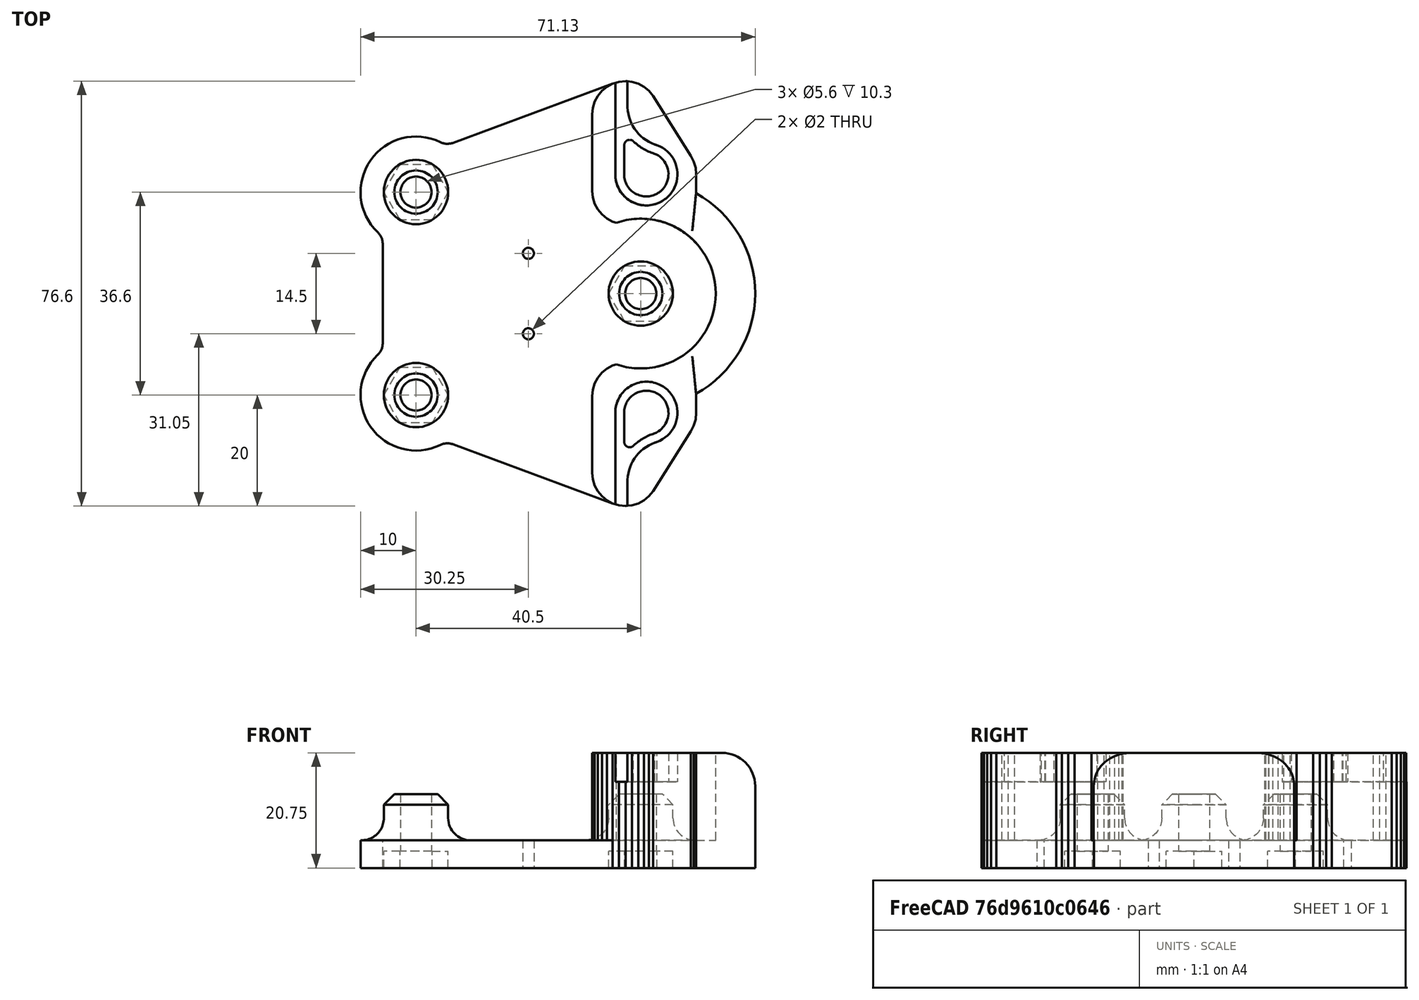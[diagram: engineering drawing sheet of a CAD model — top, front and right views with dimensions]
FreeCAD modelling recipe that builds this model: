
FCSTD DOCUMENT  (FreeCAD 0.19R24267 +99 (Git))
Label: carroX_V1
License: All rights reserved
LicenseURL: http://en.wikipedia.org/wiki/All_rights_reserved
objects: Part::Feature×137, Part::Part2DObjectPython×11, Part::Cylinder×9, Part::FeaturePython×8, Part::Cut×7, Part::MultiFuse×5, Part::Extrusion×5, Part::Prism×3, Part::Fillet×3, Part::Fuse×2, Part::Box×1, App::DocumentObjectGroupPython×1, Part::Mirroring×1, Part::Refine×1, Part::Chamfer×1
note: 194 computed .brp shape members not serialized (recipe doc carries the construction recipe); baked Part::Feature solids carry a one-line shape summary decoded from their .brp

FEATURE [Part::Feature] polygon
  shape: bbox 44.5 x 64.6 x 2e-07 mm, 1 faces, 0 solids (baked)
FEATURE [Part::Part2DObjectPython] circle  # Draft 2D object (typed FeaturePython)
  Area = 113.097
  FirstAngle = 0
  LastAngle = 0
  MakeFace = true
  Radius = 6
FEATURE [Part::FeaturePython] minkowski  # WARN: FeaturePython — macro-defined, semantics opaque (R4)
  Arguments = {'convexity': '0'}
  Children = -> [polygon,circle]
  Operation = minkowski
FEATURE [Part::Part2DObjectPython] circle001  # Draft 2D object (typed FeaturePython)
  Area = 314.159
  FirstAngle = 0
  LastAngle = 0
  MakeFace = true
  Placement = pos=(-20.25,-18.3,0) rot=(0,0,1;0rad)
  Radius = 10
FEATURE [Part::Part2DObjectPython] circle002  # Draft 2D object (typed FeaturePython)
  Area = 314.159
  FirstAngle = 0
  LastAngle = 0
  MakeFace = true
  Placement = pos=(-20.25,18.3,0) rot=(0,0,1;0rad)
  Radius = 10
FEATURE [Part::Part2DObjectPython] circle003  # Draft 2D object (typed FeaturePython)
  Area = 1336.4
  FirstAngle = 0
  LastAngle = 0
  MakeFace = true
  Placement = pos=(20.25,0,0) rot=(0,0,1;0rad)
  Radius = 20.625
FEATURE [Part::MultiFuse] union
  Shapes = -> [minkowski,circle001,circle002,circle003]
FEATURE [Part::Part2DObjectPython] circle004  # Draft 2D object (typed FeaturePython)
  Area = 24.6301
  FirstAngle = 0
  LastAngle = 0
  MakeFace = true
  Placement = pos=(-20.25,-18.3,0) rot=(0,0,1;0rad)
  Radius = 2.8
FEATURE [Part::Part2DObjectPython] circle005  # Draft 2D object (typed FeaturePython)
  Area = 24.6301
  FirstAngle = 0
  LastAngle = 0
  MakeFace = true
  Placement = pos=(20.25,0,0) rot=(0,0,1;0rad)
  Radius = 2.8
FEATURE [Part::Part2DObjectPython] circle006  # Draft 2D object (typed FeaturePython)
  Area = 24.6301
  FirstAngle = 0
  LastAngle = 0
  MakeFace = true
  Placement = pos=(-20.25,18.3,0) rot=(0,0,1;0rad)
  Radius = 2.8
FEATURE [Part::Part2DObjectPython] circle007  # Draft 2D object (typed FeaturePython)
  Area = 3.14159
  FirstAngle = 0
  LastAngle = 0
  MakeFace = true
  Placement = pos=(0,7.25,0) rot=(0,0,1;0rad)
  Radius = 1
FEATURE [Part::Part2DObjectPython] circle008  # Draft 2D object (typed FeaturePython)
  Area = 3.14159
  FirstAngle = 0
  LastAngle = 0
  MakeFace = true
  Placement = pos=(0,-7.25,0) rot=(0,0,1;0rad)
  Radius = 1
FEATURE [Part::MultiFuse] union001
  Shapes = -> [circle004,circle005,circle006,circle007,circle008]
FEATURE [Part::Cut] difference
  Base = -> union
  Tool = -> union001
FEATURE [Part::FeaturePython] RefineLinearExtrude  # WARN: FeaturePython — macro-defined, semantics opaque (R4)
  Base = -> difference
FEATURE [Part::Extrusion] LinearExtrude
  Base = -> RefineLinearExtrude
  Dir = (0,0,5)
  DirMode = 0
  FaceMakerClass = Part::FaceMakerBullseye
  LengthFwd = 0
  LengthRev = 0
  Solid = false
  Symmetric = false
FEATURE [Part::Feature] polygon001
  shape: bbox 6.75 x 13.8 x 2e-07 mm, 1 faces, 0 solids (baked)
FEATURE [Part::Part2DObjectPython] circle009  # Draft 2D object (typed FeaturePython)
  Area = 113.097
  FirstAngle = 0
  LastAngle = 0
  MakeFace = true
  Radius = 6
FEATURE [Part::FeaturePython] minkowski001  # WARN: FeaturePython — macro-defined, semantics opaque (R4)
  Arguments = {'convexity': '0'}
  Children = -> [polygon001,circle009]
  Operation = minkowski
FEATURE [Part::FeaturePython] RefineLinearExtrude001  # WARN: FeaturePython — macro-defined, semantics opaque (R4)
  Base = -> minkowski001
FEATURE [Part::Extrusion] LinearExtrude001
  Base = -> RefineLinearExtrude001
  Dir = (0,0,20.75)
  DirMode = 0
  FaceMakerClass = Part::FaceMakerBullseye
  LengthFwd = 0
  LengthRev = 0
  Solid = false
  Symmetric = false
FEATURE [Part::Feature] polygon002
  shape: bbox 6.75 x 13.8 x 2e-07 mm, 1 faces, 0 solids (baked)
FEATURE [Part::Part2DObjectPython] circle010  # Draft 2D object (typed FeaturePython)
  Area = 113.097
  FirstAngle = 0
  LastAngle = 0
  MakeFace = true
  Radius = 6
FEATURE [Part::FeaturePython] minkowski002  # WARN: FeaturePython — macro-defined, semantics opaque (R4)
  Arguments = {'convexity': '0'}
  Children = -> [polygon002,circle010]
  Operation = minkowski
FEATURE [Part::FeaturePython] RefineLinearExtrude002  # WARN: FeaturePython — macro-defined, semantics opaque (R4)
  Base = -> minkowski002
FEATURE [Part::Extrusion] LinearExtrude002
  Base = -> RefineLinearExtrude002
  Dir = (0,0,20.75)
  DirMode = 0
  FaceMakerClass = Part::FaceMakerBullseye
  LengthFwd = 0
  LengthRev = 0
  Solid = false
  Symmetric = false
FEATURE [Part::Fuse] union002
  Base = -> LinearExtrude001
  Tool = -> LinearExtrude002
FEATURE [Part::Cylinder] cylinder
  Angle = 360
  AttacherType = Attacher::AttachEngine3D
  Height = 60
  Placement = pos=(20.25,0,0) rot=(0,0,1;0rad)
  Radius = 13.5
FEATURE [Part::Cut] difference001
  Base = -> union002
  Tool = -> cylinder
FEATURE [Part::Cylinder] cylinder001
  Angle = 360
  AttacherType = Attacher::AttachEngine3D
  Height = 13.3
  Radius = 5.8
FEATURE [Part::Cylinder] cylinder002
  Angle = 360
  AttacherType = Attacher::AttachEngine3D
  Height = 53.2
  Placement = pos=(0,0,-26.6) rot=(0,0,1;0rad)
  Radius = 2.8
FEATURE [Part::Cut] difference002
  Base = -> cylinder001
  Placement = pos=(-20.25,-18.3,0) rot=(0,0,1;0rad)
  Tool = -> cylinder002
FEATURE [Part::Cylinder] cylinder003
  Angle = 360
  AttacherType = Attacher::AttachEngine3D
  Height = 13.3
  Radius = 5.8
FEATURE [Part::Cylinder] cylinder004
  Angle = 360
  AttacherType = Attacher::AttachEngine3D
  Height = 53.2
  Placement = pos=(0,0,-26.6) rot=(0,0,1;0rad)
  Radius = 2.8
FEATURE [Part::Cut] difference003
  Base = -> cylinder003
  Placement = pos=(-20.25,18.3,0) rot=(0,0,1;0rad)
  Tool = -> cylinder004
FEATURE [Part::Cylinder] cylinder005
  Angle = 360
  AttacherType = Attacher::AttachEngine3D
  Height = 13.3
  Radius = 5.8
FEATURE [Part::Cylinder] cylinder006
  Angle = 360
  AttacherType = Attacher::AttachEngine3D
  Height = 53.2
  Placement = pos=(0,0,-26.6) rot=(0,0,1;0rad)
  Radius = 2.8
FEATURE [Part::Cut] difference004
  Base = -> cylinder005
  Placement = pos=(20.25,0,0) rot=(0,0,1;0rad)
  Tool = -> cylinder006
FEATURE [Part::Cylinder] cylinder007
  Angle = 360
  AttacherType = Attacher::AttachEngine3D
  Height = 20.75
  Radius = 20.625
FEATURE [Part::Cylinder] cylinder008
  Angle = 360
  AttacherType = Attacher::AttachEngine3D
  Height = 1000
  Placement = pos=(0,0,4.99) rot=(0,0,1;0rad)
  Radius = 13.5
FEATURE [Part::Box] cube
  AttacherType = Attacher::AttachEngine3D
  Height = 1000
  Length = 1000
  Placement = pos=(-997,-500,0) rot=(0,0,1;0rad)
  Width = 1000
FEATURE [Part::Fuse] union003
  Base = -> cylinder008
  Tool = -> cube
FEATURE [Part::Cut] difference005
  Base = -> cylinder007
  Placement = pos=(20.25,0,0) rot=(0,0,1;0rad)
  Tool = -> union003
FEATURE [Part::MultiFuse] union004
  Shapes = -> [LinearExtrude,difference001,difference002,difference003,difference004,difference005]
FEATURE [Part::Prism] prism
  AttacherType = Attacher::AttachEngine3D
  Circumradius = 5.79
  FirstAngle = 0
  Height = 6
  Placement = pos=(-20.25,-18.3,-3) rot=(0,0,1;0rad)
  Polygon = 6
  SecondAngle = 0
FEATURE [Part::Prism] prism001
  AttacherType = Attacher::AttachEngine3D
  Circumradius = 5.79
  FirstAngle = 0
  Height = 6
  Placement = pos=(-20.25,18.3,-3) rot=(0,0,1;0rad)
  Polygon = 6
  SecondAngle = 0
FEATURE [Part::Prism] prism002
  AttacherType = Attacher::AttachEngine3D
  Circumradius = 5.79
  FirstAngle = 0
  Height = 6
  Placement = pos=(20.25,0,-3) rot=(0,0,1;0rad)
  Polygon = 6
  SecondAngle = 0
FEATURE [Part::MultiFuse] Group
  Shapes = -> [prism,prism001,prism002]
FEATURE [App::DocumentObjectGroupPython] LayerContainer  label="Capas"  # scripted group (container) (typed FeaturePython)
FEATURE [Part::Feature] Line
  shape: bbox 25.93 x 2e-07 x 2e-07 mm, 0 faces, 0 solids (baked)
FEATURE [Part::Feature] Line001
  shape: bbox 5.23 x 0.01028 x 2e-07 mm, 0 faces, 0 solids (baked)
FEATURE [Part::Feature] Line002
  shape: bbox 13.12 x 2e-07 x 2e-07 mm, 0 faces, 0 solids (baked)
FEATURE [Part::Feature] Line003
  shape: bbox 46.78 x 2e-07 x 2e-07 mm, 0 faces, 0 solids (baked)
FEATURE [Part::Feature] Line004
  shape: bbox 46.66 x 2e-07 x 2e-07 mm, 0 faces, 0 solids (baked)
FEATURE [Part::Feature] Line005
  shape: bbox 2e-07 x 2.2 x 2e-07 mm, 0 faces, 0 solids (baked)
FEATURE [Part::Feature] Arc
  shape: bbox 7.844 x 7.989 x 2e-07 mm, 0 faces, 0 solids (baked)
FEATURE [Part::Feature] Arc001
  shape: bbox 0.9979 x 1.743 x 2e-07 mm, 0 faces, 0 solids (baked)
FEATURE [Part::Feature] Arc002
  shape: bbox 10.99 x 11.2 x 2e-07 mm, 0 faces, 0 solids (baked)
FEATURE [Part::Feature] Arc003
  shape: bbox 2.238 x 3.76 x 2e-07 mm, 0 faces, 0 solids (baked)
FEATURE [Part::Feature] Arc004
  shape: bbox 7.439 x 5.334 x 2e-07 mm, 0 faces, 0 solids (baked)
FEATURE [Part::Feature] dxf_ToyRepCart_all
  Placement = pos=(0,0,0) rot=(0,0,1;1.5708rad)
  shape: bbox 11.2 x 78.19 x 2e-07 mm, 1 faces, 0 solids (baked)
FEATURE [Part::FeaturePython] RefineLinearExtrude003  # WARN: FeaturePython — macro-defined, semantics opaque (R4)
  Base = -> dxf_ToyRepCart_all
FEATURE [Part::Extrusion] LinearExtrude003
  Base = -> RefineLinearExtrude003
  Dir = (0,0,100)
  DirMode = 0
  FaceMakerClass = Part::FaceMakerBullseye
  LengthFwd = 0
  LengthRev = 0
  Placement = pos=(21.25,-21.5,15.55) rot=(0,0,1;0rad)
  Solid = false
  Symmetric = false
FEATURE [Part::Feature] Line006
  shape: bbox 25.93 x 2e-07 x 2e-07 mm, 0 faces, 0 solids (baked)
FEATURE [Part::Feature] Line007
  shape: bbox 5.23 x 0.01028 x 2e-07 mm, 0 faces, 0 solids (baked)
FEATURE [Part::Feature] Line008
  shape: bbox 13.12 x 2e-07 x 2e-07 mm, 0 faces, 0 solids (baked)
FEATURE [Part::Feature] Line009
  shape: bbox 46.78 x 2e-07 x 2e-07 mm, 0 faces, 0 solids (baked)
FEATURE [Part::Feature] Line010
  shape: bbox 46.66 x 2e-07 x 2e-07 mm, 0 faces, 0 solids (baked)
FEATURE [Part::Feature] Line011
  shape: bbox 2e-07 x 2.2 x 2e-07 mm, 0 faces, 0 solids (baked)
FEATURE [Part::Feature] Arc005
  shape: bbox 7.844 x 7.989 x 2e-07 mm, 0 faces, 0 solids (baked)
FEATURE [Part::Feature] Arc006
  shape: bbox 0.9979 x 1.743 x 2e-07 mm, 0 faces, 0 solids (baked)
FEATURE [Part::Feature] Arc007
  shape: bbox 10.99 x 11.2 x 2e-07 mm, 0 faces, 0 solids (baked)
FEATURE [Part::Feature] Arc008
  shape: bbox 2.238 x 3.76 x 2e-07 mm, 0 faces, 0 solids (baked)
FEATURE [Part::Feature] Arc009
  shape: bbox 7.439 x 5.334 x 2e-07 mm, 0 faces, 0 solids (baked)
FEATURE [Part::Feature] dxf_ToyRepCart_all001
  Placement = pos=(0,0,0) rot=(0,0,1;1.5708rad)
  shape: bbox 11.2 x 78.19 x 2e-07 mm, 1 faces, 0 solids (baked)
FEATURE [Part::FeaturePython] RefineLinearExtrude004  # WARN: FeaturePython — macro-defined, semantics opaque (R4)
  Base = -> dxf_ToyRepCart_all001
FEATURE [Part::Extrusion] LinearExtrude004
  Base = -> RefineLinearExtrude004
  Dir = (0,0,100)
  DirMode = 0
  FaceMakerClass = Part::FaceMakerBullseye
  LengthFwd = 0
  LengthRev = 0
  Placement = pos=(21.25,-21.5,15.55) rot=(0,0,1;0rad)
  Solid = false
  Symmetric = false
FEATURE [Part::Mirroring] mirr_LinearExtrude004  label="mirrored LinearExtrude004"
  Base = (0,0,0)
  Normal = (0,1,0)
  Source = -> LinearExtrude004
FEATURE [Part::MultiFuse] union005
  Shapes = -> [Group,LinearExtrude003,mirr_LinearExtrude004]
FEATURE [Part::Cut] difference006
  Base = -> union004
  Tool = -> union005
FEATURE [Part::Feature] Line012
  shape: bbox 1.171 x 0.1152 x 2e-07 mm, 0 faces, 0 solids (baked)
FEATURE [Part::Feature] Line013
  shape: bbox 1.171 x 0.1152 x 2e-07 mm, 0 faces, 0 solids (baked)
FEATURE [Part::Feature] Line014
  shape: bbox 1.125 x 0.3418 x 2e-07 mm, 0 faces, 0 solids (baked)
FEATURE [Part::Feature] Line015
  shape: bbox 37.75 x 14 x 2e-07 mm, 0 faces, 0 solids (baked)
FEATURE [Part::Feature] Line016
  shape: bbox 1.037 x 0.5537 x 2e-07 mm, 0 faces, 0 solids (baked)
FEATURE [Part::Feature] Line017
  shape: bbox 0.9092 x 0.7471 x 2e-07 mm, 0 faces, 0 solids (baked)
FEATURE [Part::Feature] Line018
  shape: bbox 0.7471 x 0.9092 x 2e-07 mm, 0 faces, 0 solids (baked)
FEATURE [Part::Feature] Line019
  shape: bbox 0.5537 x 1.037 x 2e-07 mm, 0 faces, 0 solids (baked)
FEATURE [Part::Feature] Line020
  shape: bbox 0.3418 x 1.125 x 2e-07 mm, 0 faces, 0 solids (baked)
FEATURE [Part::Feature] Line021
  shape: bbox 0.1152 x 1.171 x 2e-07 mm, 0 faces, 0 solids (baked)
FEATURE [Part::Feature] Line022
  shape: bbox 2e-07 x 36.6 x 2e-07 mm, 0 faces, 0 solids (baked)
FEATURE [Part::Feature] Line023
  shape: bbox 0.1152 x 1.171 x 2e-07 mm, 0 faces, 0 solids (baked)
FEATURE [Part::Feature] Line024
  shape: bbox 0.3418 x 1.125 x 2e-07 mm, 0 faces, 0 solids (baked)
FEATURE [Part::Feature] Line025
  shape: bbox 0.5537 x 1.037 x 2e-07 mm, 0 faces, 0 solids (baked)
FEATURE [Part::Feature] Line026
  shape: bbox 0.7471 x 0.9092 x 2e-07 mm, 0 faces, 0 solids (baked)
FEATURE [Part::Feature] Line027
  shape: bbox 0.9092 x 0.7471 x 2e-07 mm, 0 faces, 0 solids (baked)
FEATURE [Part::Feature] Line028
  shape: bbox 1.037 x 0.5537 x 2e-07 mm, 0 faces, 0 solids (baked)
FEATURE [Part::Feature] Line029
  shape: bbox 37.75 x 14 x 2e-07 mm, 0 faces, 0 solids (baked)
FEATURE [Part::Feature] Line030
  shape: bbox 1.125 x 0.3418 x 2e-07 mm, 0 faces, 0 solids (baked)
FEATURE [Part::Feature] Line031
  shape: bbox 1.171 x 0.1152 x 2e-07 mm, 0 faces, 0 solids (baked)
FEATURE [Part::Feature] Line032
  shape: bbox 1.171 x 0.1152 x 2e-07 mm, 0 faces, 0 solids (baked)
FEATURE [Part::Feature] Line033
  shape: bbox 1.125 x 0.3418 x 2e-07 mm, 0 faces, 0 solids (baked)
FEATURE [Part::Feature] Line034
  shape: bbox 1.037 x 0.5537 x 2e-07 mm, 0 faces, 0 solids (baked)
FEATURE [Part::Feature] Line035
  shape: bbox 0.9092 x 0.7471 x 2e-07 mm, 0 faces, 0 solids (baked)
FEATURE [Part::Feature] Line036
  shape: bbox 0.7471 x 0.9092 x 2e-07 mm, 0 faces, 0 solids (baked)
FEATURE [Part::Feature] Line037
  shape: bbox 6.75 x 10.8 x 2e-07 mm, 0 faces, 0 solids (baked)
FEATURE [Part::Feature] Line038
  shape: bbox 0.5537 x 1.037 x 2e-07 mm, 0 faces, 0 solids (baked)
FEATURE [Part::Feature] Line039
  shape: bbox 0.3418 x 1.125 x 2e-07 mm, 0 faces, 0 solids (baked)
FEATURE [Part::Feature] Line040
  shape: bbox 0.1152 x 1.171 x 2e-07 mm, 0 faces, 0 solids (baked)
FEATURE [Part::Feature] Line041
  shape: bbox 2e-07 x 43 x 2e-07 mm, 0 faces, 0 solids (baked)
FEATURE [Part::Feature] Line042
  shape: bbox 0.1152 x 1.171 x 2e-07 mm, 0 faces, 0 solids (baked)
FEATURE [Part::Feature] Line043
  shape: bbox 0.3418 x 1.125 x 2e-07 mm, 0 faces, 0 solids (baked)
FEATURE [Part::Feature] Line044
  shape: bbox 0.5537 x 1.037 x 2e-07 mm, 0 faces, 0 solids (baked)
FEATURE [Part::Feature] Line045
  shape: bbox 6.75 x 10.8 x 2e-07 mm, 0 faces, 0 solids (baked)
FEATURE [Part::Feature] Line046
  shape: bbox 0.7471 x 0.9092 x 2e-07 mm, 0 faces, 0 solids (baked)
FEATURE [Part::Feature] Line047
  shape: bbox 0.9092 x 0.7471 x 2e-07 mm, 0 faces, 0 solids (baked)
FEATURE [Part::Feature] Line048
  shape: bbox 1.037 x 0.5537 x 2e-07 mm, 0 faces, 0 solids (baked)
FEATURE [Part::Feature] Line049
  shape: bbox 1.125 x 0.3418 x 2e-07 mm, 0 faces, 0 solids (baked)
FEATURE [Part::Feature] Line050
  shape: bbox 1.125 x 0.3418 x 2e-07 mm, 0 faces, 0 solids (baked)
FEATURE [Part::Feature] Line051
  shape: bbox 1.171 x 0.1152 x 2e-07 mm, 0 faces, 0 solids (baked)
FEATURE [Part::Feature] Line052
  shape: bbox 1.171 x 0.1152 x 2e-07 mm, 0 faces, 0 solids (baked)
FEATURE [Part::Feature] Line053
  shape: bbox 1.125 x 0.3418 x 2e-07 mm, 0 faces, 0 solids (baked)
FEATURE [Part::Feature] Line054
  shape: bbox 1.037 x 0.5537 x 2e-07 mm, 0 faces, 0 solids (baked)
FEATURE [Part::Feature] Line055
  shape: bbox 0.9092 x 0.7471 x 2e-07 mm, 0 faces, 0 solids (baked)
FEATURE [Part::Feature] Line056
  shape: bbox 0.7471 x 0.9092 x 2e-07 mm, 0 faces, 0 solids (baked)
FEATURE [Part::Feature] Line057
  shape: bbox 0.5537 x 1.037 x 2e-07 mm, 0 faces, 0 solids (baked)
FEATURE [Part::Feature] Line058
  shape: bbox 0.3418 x 1.125 x 2e-07 mm, 0 faces, 0 solids (baked)
FEATURE [Part::Feature] Line059
  shape: bbox 0.1152 x 1.171 x 2e-07 mm, 0 faces, 0 solids (baked)
FEATURE [Part::Feature] Line060
  shape: bbox 2e-07 x 13.8 x 2e-07 mm, 0 faces, 0 solids (baked)
FEATURE [Part::Feature] Line061
  shape: bbox 0.1152 x 1.171 x 2e-07 mm, 0 faces, 0 solids (baked)
FEATURE [Part::Feature] Line062
  shape: bbox 0.3418 x 1.125 x 2e-07 mm, 0 faces, 0 solids (baked)
FEATURE [Part::Feature] Line063
  shape: bbox 0.5537 x 1.037 x 2e-07 mm, 0 faces, 0 solids (baked)
FEATURE [Part::Feature] Line064
  shape: bbox 0.7471 x 0.9092 x 2e-07 mm, 0 faces, 0 solids (baked)
FEATURE [Part::Feature] Line065
  shape: bbox 0.9092 x 0.7471 x 2e-07 mm, 0 faces, 0 solids (baked)
FEATURE [Part::Feature] Line066
  shape: bbox 1.037 x 0.5537 x 2e-07 mm, 0 faces, 0 solids (baked)
FEATURE [Part::Feature] Line067
  shape: bbox 1.125 x 0.3418 x 2e-07 mm, 0 faces, 0 solids (baked)
FEATURE [Part::Feature] Line068
  shape: bbox 1.171 x 0.1152 x 2e-07 mm, 0 faces, 0 solids (baked)
FEATURE [Part::Feature] Line069
  shape: bbox 6.75 x 2e-07 x 2e-07 mm, 0 faces, 0 solids (baked)
FEATURE [Part::Feature] Line070
  shape: bbox 1.171 x 0.1152 x 2e-07 mm, 0 faces, 0 solids (baked)
FEATURE [Part::Feature] Line071
  shape: bbox 1.125 x 0.3418 x 2e-07 mm, 0 faces, 0 solids (baked)
FEATURE [Part::Feature] Line072
  shape: bbox 1.037 x 0.5537 x 2e-07 mm, 0 faces, 0 solids (baked)
FEATURE [Part::Feature] Line073
  shape: bbox 0.9092 x 0.7471 x 2e-07 mm, 0 faces, 0 solids (baked)
FEATURE [Part::Feature] Line074
  shape: bbox 0.7471 x 0.9092 x 2e-07 mm, 0 faces, 0 solids (baked)
FEATURE [Part::Feature] Line075
  shape: bbox 0.5537 x 1.037 x 2e-07 mm, 0 faces, 0 solids (baked)
FEATURE [Part::Feature] Line076
  shape: bbox 0.3418 x 1.125 x 2e-07 mm, 0 faces, 0 solids (baked)
FEATURE [Part::Feature] Line077
  shape: bbox 0.1152 x 1.171 x 2e-07 mm, 0 faces, 0 solids (baked)
FEATURE [Part::Feature] Line078
  shape: bbox 2e-07 x 3 x 2e-07 mm, 0 faces, 0 solids (baked)
FEATURE [Part::Feature] Line079
  shape: bbox 0.1152 x 1.171 x 2e-07 mm, 0 faces, 0 solids (baked)
FEATURE [Part::Feature] Line080
  shape: bbox 0.3418 x 1.125 x 2e-07 mm, 0 faces, 0 solids (baked)
FEATURE [Part::Feature] Line081
  shape: bbox 0.5537 x 1.037 x 2e-07 mm, 0 faces, 0 solids (baked)
FEATURE [Part::Feature] Line082
  shape: bbox 6.75 x 10.8 x 2e-07 mm, 0 faces, 0 solids (baked)
FEATURE [Part::Feature] Line083
  shape: bbox 0.7471 x 0.9092 x 2e-07 mm, 0 faces, 0 solids (baked)
FEATURE [Part::Feature] Line084
  shape: bbox 0.9092 x 0.7471 x 2e-07 mm, 0 faces, 0 solids (baked)
FEATURE [Part::Feature] Line085
  shape: bbox 1.037 x 0.5537 x 2e-07 mm, 0 faces, 0 solids (baked)
FEATURE [Part::Feature] Line086
  shape: bbox 0.7471 x 0.9092 x 2e-07 mm, 0 faces, 0 solids (baked)
FEATURE [Part::Feature] Line087
  shape: bbox 0.9092 x 0.7471 x 2e-07 mm, 0 faces, 0 solids (baked)
FEATURE [Part::Feature] Line088
  shape: bbox 1.037 x 0.5537 x 2e-07 mm, 0 faces, 0 solids (baked)
FEATURE [Part::Feature] Line089
  shape: bbox 1.125 x 0.3418 x 2e-07 mm, 0 faces, 0 solids (baked)
FEATURE [Part::Feature] Line090
  shape: bbox 1.171 x 0.1152 x 2e-07 mm, 0 faces, 0 solids (baked)
FEATURE [Part::Feature] Line091
  shape: bbox 6.75 x 2e-07 x 2e-07 mm, 0 faces, 0 solids (baked)
FEATURE [Part::Feature] Line092
  shape: bbox 1.171 x 0.1152 x 2e-07 mm, 0 faces, 0 solids (baked)
FEATURE [Part::Feature] Line093
  shape: bbox 1.125 x 0.3418 x 2e-07 mm, 0 faces, 0 solids (baked)
FEATURE [Part::Feature] Line094
  shape: bbox 1.037 x 0.5537 x 2e-07 mm, 0 faces, 0 solids (baked)
FEATURE [Part::Feature] Line095
  shape: bbox 0.9092 x 0.7471 x 2e-07 mm, 0 faces, 0 solids (baked)
FEATURE [Part::Feature] Line096
  shape: bbox 0.7471 x 0.9092 x 2e-07 mm, 0 faces, 0 solids (baked)
FEATURE [Part::Feature] Line097
  shape: bbox 0.5537 x 1.037 x 2e-07 mm, 0 faces, 0 solids (baked)
FEATURE [Part::Feature] Line098
  shape: bbox 0.3418 x 1.125 x 2e-07 mm, 0 faces, 0 solids (baked)
FEATURE [Part::Feature] Line099
  shape: bbox 0.1152 x 1.171 x 2e-07 mm, 0 faces, 0 solids (baked)
FEATURE [Part::Feature] Line100
  shape: bbox 2e-07 x 13.8 x 2e-07 mm, 0 faces, 0 solids (baked)
FEATURE [Part::Feature] Line101
  shape: bbox 0.1152 x 1.171 x 2e-07 mm, 0 faces, 0 solids (baked)
FEATURE [Part::Feature] Line102
  shape: bbox 0.3418 x 1.125 x 2e-07 mm, 0 faces, 0 solids (baked)
FEATURE [Part::Feature] Line103
  shape: bbox 0.5537 x 1.037 x 2e-07 mm, 0 faces, 0 solids (baked)
FEATURE [Part::Feature] Line104
  shape: bbox 0.7471 x 0.9092 x 2e-07 mm, 0 faces, 0 solids (baked)
FEATURE [Part::Feature] Line105
  shape: bbox 0.9092 x 0.7471 x 2e-07 mm, 0 faces, 0 solids (baked)
FEATURE [Part::Feature] Line106
  shape: bbox 1.037 x 0.5537 x 2e-07 mm, 0 faces, 0 solids (baked)
FEATURE [Part::Feature] Line107
  shape: bbox 1.125 x 0.3418 x 2e-07 mm, 0 faces, 0 solids (baked)
FEATURE [Part::Feature] Line108
  shape: bbox 1.171 x 0.1152 x 2e-07 mm, 0 faces, 0 solids (baked)
FEATURE [Part::Feature] Line109
  shape: bbox 1.171 x 0.1152 x 2e-07 mm, 0 faces, 0 solids (baked)
FEATURE [Part::Feature] Line110
  shape: bbox 1.125 x 0.3418 x 2e-07 mm, 0 faces, 0 solids (baked)
FEATURE [Part::Feature] Line111
  shape: bbox 1.037 x 0.5537 x 2e-07 mm, 0 faces, 0 solids (baked)
FEATURE [Part::Feature] Line112
  shape: bbox 0.9092 x 0.7471 x 2e-07 mm, 0 faces, 0 solids (baked)
FEATURE [Part::Feature] Line113
  shape: bbox 0.7471 x 0.9092 x 2e-07 mm, 0 faces, 0 solids (baked)
FEATURE [Part::Feature] Line114
  shape: bbox 6.75 x 10.8 x 2e-07 mm, 0 faces, 0 solids (baked)
FEATURE [Part::Feature] Line115
  shape: bbox 0.5537 x 1.037 x 2e-07 mm, 0 faces, 0 solids (baked)
FEATURE [Part::Feature] Line116
  shape: bbox 0.3418 x 1.125 x 2e-07 mm, 0 faces, 0 solids (baked)
FEATURE [Part::Feature] Line117
  shape: bbox 0.1152 x 1.171 x 2e-07 mm, 0 faces, 0 solids (baked)
FEATURE [Part::Feature] Line118
  shape: bbox 2e-07 x 3 x 2e-07 mm, 0 faces, 0 solids (baked)
FEATURE [Part::Feature] Line119
  shape: bbox 0.1152 x 1.171 x 2e-07 mm, 0 faces, 0 solids (baked)
FEATURE [Part::Feature] Line120
  shape: bbox 0.3418 x 1.125 x 2e-07 mm, 0 faces, 0 solids (baked)
FEATURE [Part::Feature] Line121
  shape: bbox 0.5537 x 1.037 x 2e-07 mm, 0 faces, 0 solids (baked)
FEATURE [Part::Refine] difference006001
  Source = -> difference006
FEATURE [Part::Chamfer] Chamfer
  Base = -> difference006001
  Edges = 3 edges r=1.9: [Edge344,Edge347,Edge350]
FEATURE [Part::Fillet] Fillet
  Base = -> Chamfer
  Edges = 3 edges r=4: [Edge3,Edge47,Edge48]
FEATURE [Part::Fillet] Fillet001
  Base = -> Fillet
  Edges = 1 edges r=6: [Edge179]
FEATURE [Part::Fillet] Fillet002
  Base = -> Fillet001
  Edges = 4 edges r=3: [Edge281,Edge296,Edge297,Edge298]
